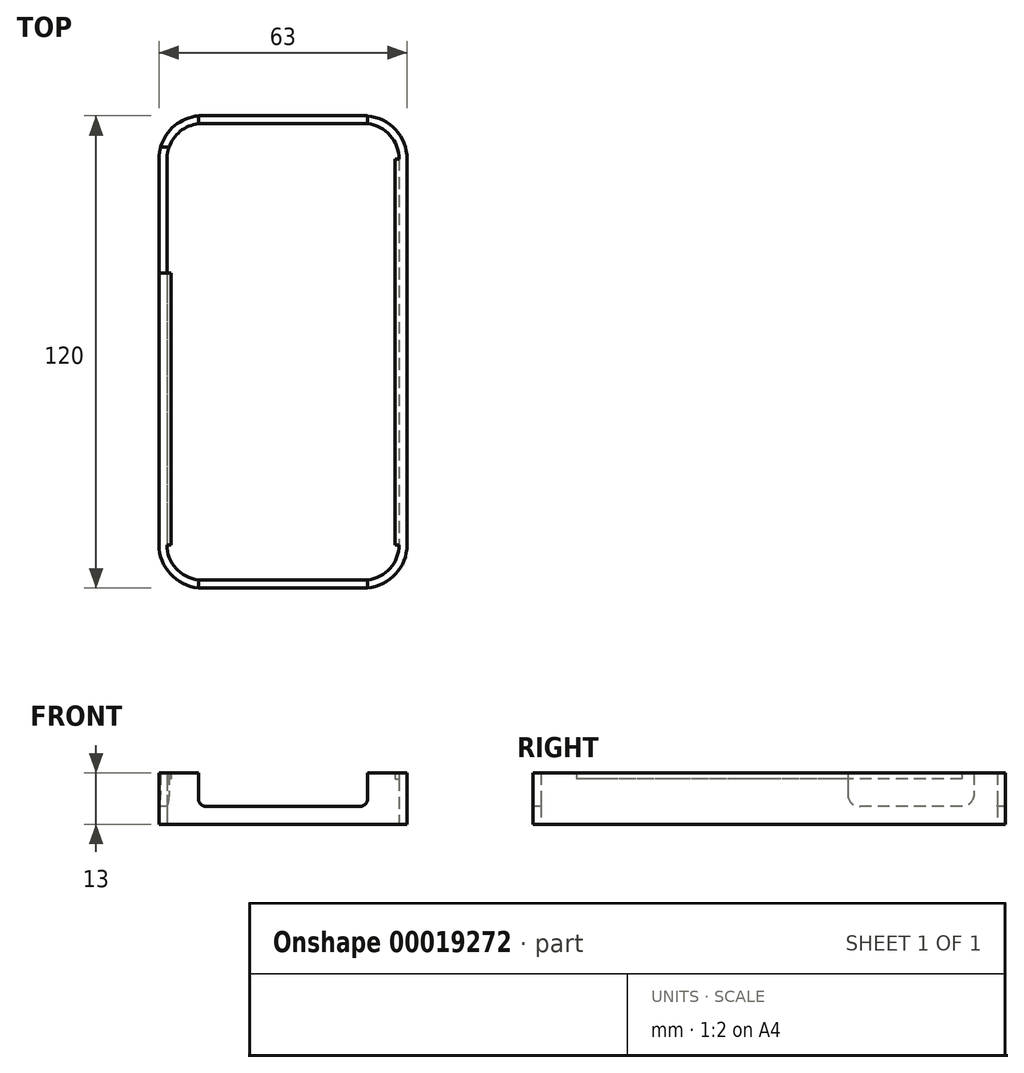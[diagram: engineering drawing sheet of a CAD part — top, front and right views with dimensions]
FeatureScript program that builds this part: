
annotation { "Feature Type Name" : "Feature", "Feature Type Description" : "" }
export const myFeature = defineFeature(function(context is Context, id is Id, definition is map)
    precondition{}
    {
        {
            var Q0;
            Q0=qCreatedBy(makeId("Top.planeOp"),FACE);
            var sketch = newSketch(context, id + "F0", { "sketchPlane" : qUnion([Q0])});
            skLineSegment(sketch, "E0.bottom", {"start": v(-23.03, 51.46) * mm, "end": v(17.97, 51.46) * mm});
            skLineSegment(sketch, "E0.top", {"start": v(-23.03, -68.54) * mm, "end": v(17.97, -68.54) * mm});
            skLineSegment(sketch, "E0.left", {"start": v(-34.03, 40.46) * mm, "end": v(-34.03, -57.54) * mm});
            skLineSegment(sketch, "E0.right", {"start": v(28.97, 40.46) * mm, "end": v(28.97, -57.54) * mm});
            skLineSegment(sketch, "E1.bottom", {"start": v(-23.03, 49.46) * mm, "end": v(17.97, 49.46) * mm});
            skLineSegment(sketch, "E1.top", {"start": v(-23.03, -66.54) * mm, "end": v(17.97, -66.54) * mm});
            skLineSegment(sketch, "E1.left", {"start": v(-32.03, 40.46) * mm, "end": v(-32.03, -57.54) * mm});
            skLineSegment(sketch, "E1.right", {"start": v(26.97, 40.46) * mm, "end": v(26.97, -57.54) * mm});
            skPoint(sketch, "E2.visualSharp", {"position": v(-34.03, 51.46) * mm});
            skArc(sketch, "E2.filletArc", {"start": v(-23.03, 51.46) * mm, "mid": v(-30.81, 48.24) * mm, "end": v(-34.03, 40.46) * mm});
            skPoint(sketch, "E3.visualSharp", {"position": v(28.97, 51.46) * mm});
            skArc(sketch, "E3.filletArc", {"start": v(28.97, 40.46) * mm, "mid": v(25.75, 48.24) * mm, "end": v(17.97, 51.46) * mm});
            skPoint(sketch, "E4.visualSharp", {"position": v(-34.03, -68.54) * mm});
            skArc(sketch, "E4.filletArc", {"start": v(-34.03, -57.54) * mm, "mid": v(-30.81, -65.32) * mm, "end": v(-23.03, -68.54) * mm});
            skPoint(sketch, "E5.visualSharp", {"position": v(28.97, -68.54) * mm});
            skArc(sketch, "E5.filletArc", {"start": v(17.97, -68.54) * mm, "mid": v(25.75, -65.32) * mm, "end": v(28.97, -57.54) * mm});
            skPoint(sketch, "E6.visualSharp", {"position": v(-32.03, 49.46) * mm});
            skArc(sketch, "E6.filletArc", {"start": v(-23.03, 49.46) * mm, "mid": v(-29.4, 46.82) * mm, "end": v(-32.03, 40.46) * mm});
            skPoint(sketch, "E7.visualSharp", {"position": v(26.97, 49.46) * mm});
            skArc(sketch, "E7.filletArc", {"start": v(26.97, 40.46) * mm, "mid": v(24.33, 46.82) * mm, "end": v(17.97, 49.46) * mm});
            skPoint(sketch, "E8.visualSharp", {"position": v(26.97, -66.54) * mm});
            skArc(sketch, "E8.filletArc", {"start": v(17.97, -66.54) * mm, "mid": v(24.33, -63.9) * mm, "end": v(26.97, -57.54) * mm});
            skPoint(sketch, "E9.visualSharp", {"position": v(-32.03, -66.54) * mm});
            skArc(sketch, "E9.filletArc", {"start": v(-32.03, -57.54) * mm, "mid": v(-29.4, -63.9) * mm, "end": v(-23.03, -66.54) * mm});
            skSolve(sketch);
        }
        {
            var Q0;
            Q0 = qSketchRegion(id + "F0", true);
            extrude(context, id + "F1", {"entities" : qUnion([Q0]), "depth" : 13 * mm});
        }
        {
            var Q0;
            Q0=makeQuery(id+"F1.opExtrude","SWEPT_FACE",FACE,{"disambiguationData":[OSD([sQuery(id+"F0.wireOp",EDGE,"E0.left")])]});
            var sketch = newSketch(context, id + "F2", { "sketchPlane" : qUnion([Q0])});
            skLineSegment(sketch, "E10.bottom", {"start": v(-43.46, 13) * mm, "end": v(-11.46, 13) * mm});
            skLineSegment(sketch, "E10.top", {"start": v(-40.46, 4.5) * mm, "end": v(-14.46, 4.5) * mm});
            skLineSegment(sketch, "E10.left", {"start": v(-43.46, 13) * mm, "end": v(-43.46, 7.5) * mm});
            skLineSegment(sketch, "E10.right", {"start": v(-11.46, 13) * mm, "end": v(-11.46, 7.5) * mm});
            skPoint(sketch, "E11.visualSharp", {"position": v(-43.46, 4.5) * mm});
            skArc(sketch, "E11.filletArc", {"start": v(-43.46, 7.5) * mm, "mid": v(-42.58, 5.38) * mm, "end": v(-40.46, 4.5) * mm});
            skPoint(sketch, "E12.visualSharp", {"position": v(-11.46, 4.5) * mm});
            skArc(sketch, "E12.filletArc", {"start": v(-14.46, 4.5) * mm, "mid": v(-12.34, 5.38) * mm, "end": v(-11.46, 7.5) * mm});
            skSolve(sketch);
        }
        {
            var Q0;
            Q0 = qSketchRegion(id + "F2", true);
            extrude(context, id + "F3", {"entities" : qUnion([Q0]), "operationType" : NewBodyOperationType.REMOVE, "endBound" : BoundingType.UP_TO_NEXT, "oppositeDirection" : true, "depth" : 25 * mm});
        }
        {
            var Q0;
            Q0=makeQuery(id+"F1.opExtrude","SWEPT_FACE",FACE,{"disambiguationData":[OSD([sQuery(id+"F0.wireOp",EDGE,"E0.top")])]});
            var sketch = newSketch(context, id + "F4", { "sketchPlane" : qUnion([Q0])});
            skLineSegment(sketch, "E13.bottom", {"start": v(-24.03, 13) * mm, "end": v(18.97, 13) * mm});
            skLineSegment(sketch, "E13.top", {"start": v(-22.03, 4.5) * mm, "end": v(16.97, 4.5) * mm});
            skLineSegment(sketch, "E13.left", {"start": v(-24.03, 13) * mm, "end": v(-24.03, 6.5) * mm});
            skLineSegment(sketch, "E13.right", {"start": v(18.97, 13) * mm, "end": v(18.97, 6.5) * mm});
            skPoint(sketch, "E14.visualSharp", {"position": v(-24.03, 4.5) * mm});
            skArc(sketch, "E14.filletArc", {"start": v(-24.03, 6.5) * mm, "mid": v(-23.45, 5.09) * mm, "end": v(-22.03, 4.5) * mm});
            skPoint(sketch, "E15.visualSharp", {"position": v(18.97, 4.5) * mm});
            skArc(sketch, "E15.filletArc", {"start": v(16.97, 4.5) * mm, "mid": v(18.38, 5.09) * mm, "end": v(18.97, 6.5) * mm});
            skSolve(sketch);
        }
        {
            var Q0;
            Q0 = qSketchRegion(id + "F4", true);
            extrude(context, id + "F5", {"entities" : qUnion([Q0]), "operationType" : NewBodyOperationType.REMOVE, "endBound" : BoundingType.THROUGH_ALL, "oppositeDirection" : true, "depth" : 25 * mm});
        }
        {
            var Q0;
            Q0=makeQuery(id+"F1.opExtrude","SWEPT_FACE",FACE,{"disambiguationData":[OSD([sQuery(id+"F0.wireOp",EDGE,"E1.left")])]});
            var sketch = newSketch(context, id + "F6", { "sketchPlane" : qUnion([Q0])});
            skLineSegment(sketch, "E16.bottom", {"start": v(11.46, 13) * mm, "end": v(-57.54, 13) * mm});
            skLineSegment(sketch, "E16.top", {"start": v(11.46, 11.5) * mm, "end": v(-57.54, 11.5) * mm});
            skLineSegment(sketch, "E16.left", {"start": v(11.46, 13) * mm, "end": v(11.46, 11.5) * mm});
            skLineSegment(sketch, "E16.right", {"start": v(-57.54, 13) * mm, "end": v(-57.54, 11.5) * mm});
            skSolve(sketch);
        }
        {
            var Q0;
            Q0 = qSketchRegion(id + "F6", true);
            extrude(context, id + "F7", {"entities" : qUnion([Q0]), "operationType" : NewBodyOperationType.ADD, "depth" : 1 * mm});
        }
        {
            var Q0;
            Q0=makeQuery(id+"F1.opExtrude","SWEPT_FACE",FACE,{"disambiguationData":[OSD([sQuery(id+"F0.wireOp",EDGE,"E1.right")])]});
            var sketch = newSketch(context, id + "F8", { "sketchPlane" : qUnion([Q0])});
            skLineSegment(sketch, "E17.bottom", {"start": v(-40.46, 13) * mm, "end": v(57.54, 13) * mm});
            skLineSegment(sketch, "E17.top", {"start": v(-40.46, 11.5) * mm, "end": v(57.54, 11.5) * mm});
            skLineSegment(sketch, "E17.left", {"start": v(-40.46, 13) * mm, "end": v(-40.46, 11.5) * mm});
            skLineSegment(sketch, "E17.right", {"start": v(57.54, 13) * mm, "end": v(57.54, 11.5) * mm});
            skSolve(sketch);
        }
        {
            var Q0;
            Q0 = qSketchRegion(id + "F8", true);
            extrude(context, id + "F9", {"entities" : qUnion([Q0]), "operationType" : NewBodyOperationType.ADD, "depth" : 1 * mm});
        }
    });
